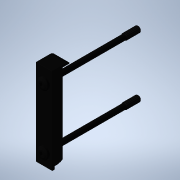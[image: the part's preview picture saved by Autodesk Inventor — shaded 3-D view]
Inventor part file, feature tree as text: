
AUTODESK INVENTOR PART (.ipt)
format: ipt  version: 2024.3 (Build 283343000, 343)  size: 283,648 bytes
history: native  units: mm
features: other x28, sketch x9, extrude x5, revolve x4, thread x2
ambient origin geometry x8: Origin, YZ Plane, XZ Plane, XY Plane, X Axis, Y Axis, Z Axis, Center Point
bodies: Solid1 (feature_tree)
feature tree (48):
  extrude  "Extrusion1"  TaperAngle=360.0deg  [1 undecoded]
  revolve  "Revolution1"  [1 undecoded]
  revolve  "Revolution2"  [1 undecoded]
  extrude  "Extrusion2"  Depth=6.6935mm TaperAngle=0.0deg
  revolve  "Revolution3"  [1 undecoded]
  thread  "Thread1"  [1 undecoded]
  revolve  "Revolution4"  [1 undecoded]
  thread  "Thread2"  [1 undecoded]
  extrude  "Extrusion3"  [1 undecoded]
  extrude  "Extrusion4"  [1 undecoded]
  extrude  "Extrusion5"  [1 undecoded]
  other  "ANBAU_XY"
  other  "ANBAU_YZ"
  other  "ANBAU_ZX"
  other  "ANBAU_X"
  other  "ANBAU_Y"
  other  "ANBAU_Z"
  other  "ANBAU_Center"
  other  "ANBAU_2_XY"
  other  "ANBAU_2_YZ"
  other  "ANBAU_2_ZX"
  other  "ANBAU_2_X"
  other  "ANBAU_2_Y"
  other  "ANBAU_2_Z"
  other  "ANBAU_2_Center"
  other  "IP_ANBAU_XY"
  other  "IP_ANBAU_YZ"
  other  "IP_ANBAU_ZX"
  other  "IP_ANBAU_X"
  other  "IP_ANBAU_Y"
  other  "IP_ANBAU_Z"
  other  "IP_ANBAU_Center"
  other  "IP_ANBAU_2_XY"
  other  "IP_ANBAU_2_YZ"
  other  "IP_ANBAU_2_ZX"
  other  "IP_ANBAU_2_X"
  other  "IP_ANBAU_2_Y"
  other  "IP_ANBAU_2_Z"
  other  "IP_ANBAU_2_Center"
  sketch  "Sketch_1"  dims[d0=8.0mm d1=0.0mm d2=360.0deg]
  sketch  "Sketch_2"  dims[d3=360.0deg d4=42.8mm d5=0.0mm]
  sketch  "Sketch_3"  dims[d6=360.0deg d7=6.6935mm d8=0.0mm]
  sketch  "Sketch_6"
  sketch  "Sketch_4"  dims[d9=360.0deg d10=6.6935mm d11=0.0mm]
  sketch  "Sketch_5"  dims[d12=1.04mm d13=0.0mm d14=1.04mm d15=0.0mm d16=4.0mm d17=0.0mm]
  sketch  "Sketch_7"
  sketch  "Sketch_8"
  sketch  "Sketch_9"
note: 10 required parameter values undecoded (feature->parameter linkage not recoverable at this tier; creation-order binding heuristic only, values carry confidence <= 0.55)